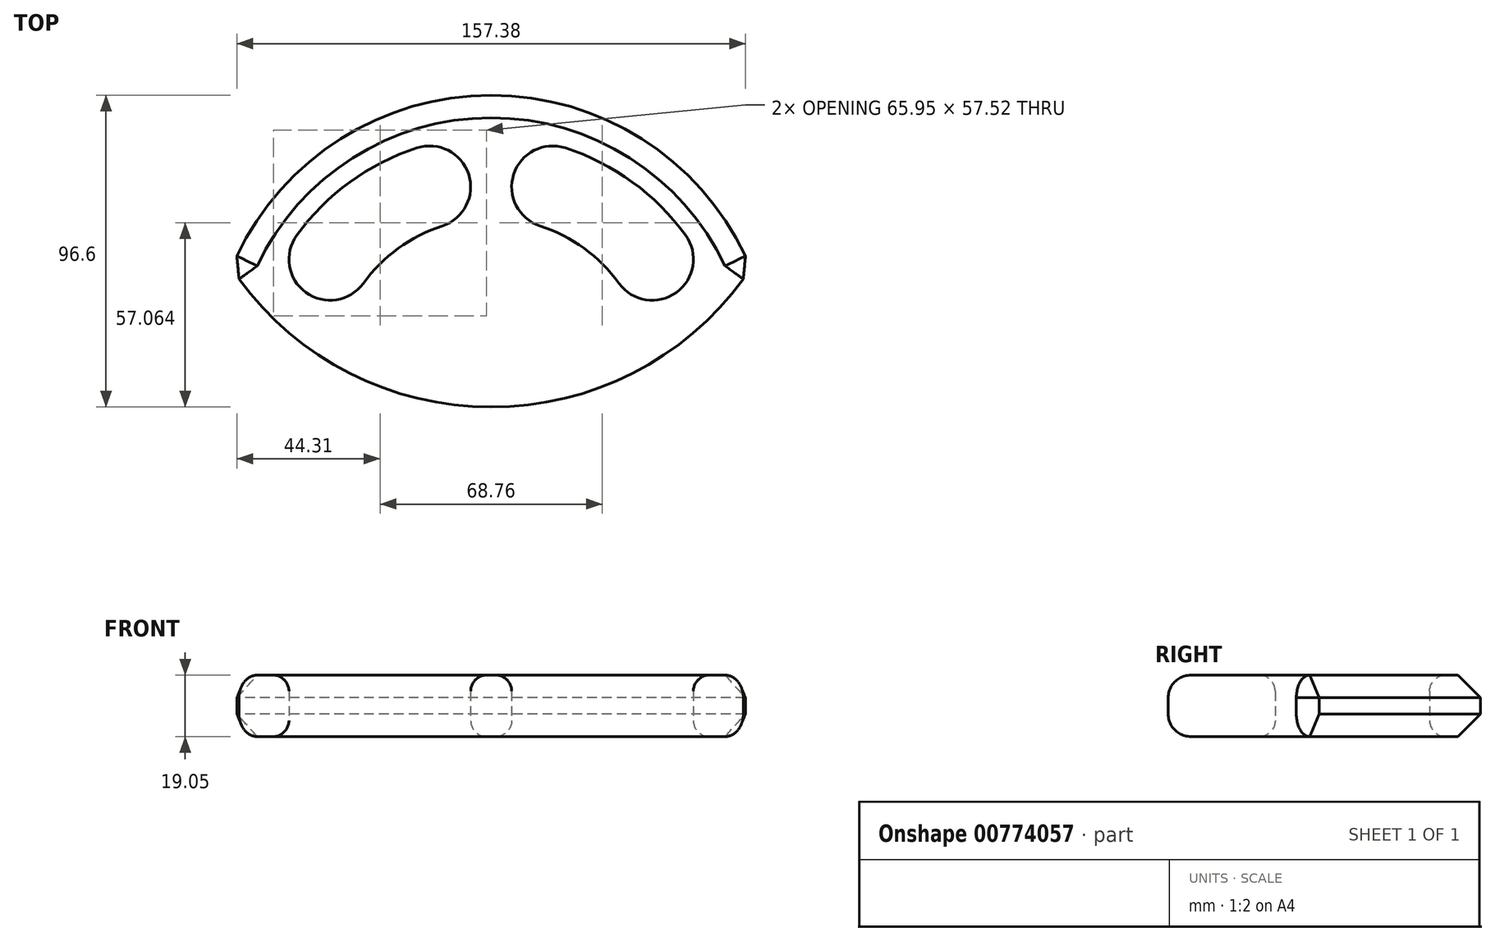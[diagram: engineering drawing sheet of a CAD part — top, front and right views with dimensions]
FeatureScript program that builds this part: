
annotation { "Feature Type Name" : "Feature", "Feature Type Description" : "" }
export const myFeature = defineFeature(function(context is Context, id is Id, definition is map)
    precondition{}
    {
        {
            var Q0;
            Q0=qCreatedBy(makeId("Top.planeOp"),FACE);
            var sketch = newSketch(context, id + "F0", { "sketchPlane" : qUnion([Q0])});
            skCircle(sketch, "E0.cCircle", {"center": v(0, 0) * mm, "radius": 61.65 * mm, "construction": true});
            skLineSegment(sketch, "E0.0", {"start": v(61.65, 0) * mm, "end": v(49.87, -36.24) * mm});
            skLineSegment(sketch, "E0.1", {"start": v(49.87, -36.24) * mm, "end": v(19.05, -58.63) * mm});
            skLineSegment(sketch, "E0.2", {"start": v(19.05, -58.63) * mm, "end": v(-19.05, -58.63) * mm});
            skLineSegment(sketch, "E0.3", {"start": v(-19.05, -58.63) * mm, "end": v(-49.87, -36.24) * mm});
            skLineSegment(sketch, "E0.4", {"start": v(-49.87, -36.24) * mm, "end": v(-61.65, 0) * mm});
            skLineSegment(sketch, "E0.5", {"start": v(-61.65, 0) * mm, "end": v(-49.87, 36.24) * mm});
            skLineSegment(sketch, "E0.6", {"start": v(-49.87, 36.24) * mm, "end": v(-19.05, 58.63) * mm});
            skLineSegment(sketch, "E0.7", {"start": v(-19.05, 58.63) * mm, "end": v(19.05, 58.63) * mm});
            skLineSegment(sketch, "E0.8", {"start": v(19.05, 58.63) * mm, "end": v(49.87, 36.24) * mm});
            skLineSegment(sketch, "E0.9", {"start": v(49.87, 36.24) * mm, "end": v(61.65, 0) * mm});
            skCircle(sketch, "E1", {"center": v(-19.05, 58.63) * mm, "radius": 12.7 * mm});
            skCircle(sketch, "E2", {"center": v(19.05, 58.63) * mm, "radius": 12.7 * mm});
            skCircle(sketch, "E3", {"center": v(-49.87, 36.24) * mm, "radius": 12.7 * mm});
            skCircle(sketch, "E4", {"center": v(49.87, 36.24) * mm, "radius": 12.7 * mm});
            skCircle(sketch, "E5", {"center": v(0, 0) * mm, "radius": 48.95 * mm});
            skCircle(sketch, "E6", {"center": v(0, 0) * mm, "radius": 74.35 * mm});
            skCircle(sketch, "E7", {"center": v(0, 0) * mm, "radius": 87.05 * mm});
            skCircle(sketch, "E8", {"center": v(0, 0) * mm, "radius": 36.25 * mm});
            skCircle(sketch, "E9", {"center": v(-49.87, 36.24) * mm, "radius": 25.4 * mm});
            skCircle(sketch, "E10", {"center": v(49.87, 36.24) * mm, "radius": 25.4 * mm});
            skCircle(sketch, "E11", {"center": v(0, 87.05) * mm, "radius": 96.6 * mm});
            skSolve(sketch);
        }
        {
            var Q0;
            {var subQ0=sQuery(id+"F0.wireOp",EDGE,"E5");var subQ8=makeQuery(id+"F0.imprint","INTERSECT",VERTEX,{"derivedFrom":[sQuery(id+"F0.wireOp",EDGE,"E2"),subQ0]});Q0=makeQuery(id+"F0.imprint","IMPRINT",FACE,{"disambiguationData":[TD([[makeQuery(id+"F0.imprint","IMPRINT",EDGE,{"disambiguationData":[TD([[subQ8,1.0]])],"derivedFrom":subQ0}),1.0]])]});}
            var Q1;
            {var subQ5=sQuery(id+"F0.wireOp",EDGE,"E6");var subQ9=makeQuery(id+"F0.imprint","INTERSECT",VERTEX,{"derivedFrom":[sQuery(id+"F0.wireOp",EDGE,"E2"),subQ5]});Q1=makeQuery(id+"F0.imprint","IMPRINT",FACE,{"disambiguationData":[TD([[makeQuery(id+"F0.imprint","IMPRINT",EDGE,{"disambiguationData":[TD([[subQ9,1.0]])],"derivedFrom":subQ5}),-1.0]])]});}
            var Q2;
            {var subQ0=sQuery(id+"F0.wireOp",EDGE,"E1");var subQ1=sQuery(id+"F0.wireOp",EDGE,"E0.7");var subQ2=makeQuery(id+"F0.imprint","INTERSECT",VERTEX,{"derivedFrom":[subQ1,subQ0]});Q2=makeQuery(id+"F0.imprint","IMPRINT",FACE,{"disambiguationData":[TD([[makeQuery(id+"F0.imprint","IMPRINT",EDGE,{"disambiguationData":[TD([[subQ2,-1.0]])],"derivedFrom":subQ1}),-1.0]])]});}
            var Q3;
            {var subQ0=sQuery(id+"F0.wireOp",EDGE,"E1");var subQ1=sQuery(id+"F0.wireOp",EDGE,"E0.7");var subQ2=makeQuery(id+"F0.imprint","INTERSECT",VERTEX,{"derivedFrom":[subQ1,subQ0]});Q3=makeQuery(id+"F0.imprint","IMPRINT",FACE,{"disambiguationData":[TD([[makeQuery(id+"F0.imprint","IMPRINT",EDGE,{"disambiguationData":[TD([[subQ2,-1.0]])],"derivedFrom":subQ1}),1.0]])]});}
            var Q4;
            {var subQ0=sQuery(id+"F0.wireOp",EDGE,"E5");var subQ1=makeQuery(id+"F0.imprint","INTERSECT",VERTEX,{"derivedFrom":[sQuery(id+"F0.wireOp",EDGE,"E3"),subQ0]});Q4=makeQuery(id+"F0.imprint","IMPRINT",FACE,{"disambiguationData":[TD([[makeQuery(id+"F0.imprint","IMPRINT",EDGE,{"disambiguationData":[TD([[subQ1,1.0]])],"derivedFrom":subQ0}),1.0]])]});}
            var Q5;
            {var subQ0=sQuery(id+"F0.wireOp",EDGE,"E9");var subQ1=sQuery(id+"F0.wireOp",EDGE,"E5");var subQ2=makeQuery(id+"F0.imprint","INTERSECT",VERTEX,{"disambiguationData":[OD(1.0)],"derivedFrom":[subQ1,subQ0]});Q5=makeQuery(id+"F0.imprint","IMPRINT",FACE,{"disambiguationData":[TD([[makeQuery(id+"F0.imprint","IMPRINT",EDGE,{"disambiguationData":[TD([[subQ2,-1.0]])],"derivedFrom":subQ1}),1.0]])]});}
            var Q6;
            {var subQ0=sQuery(id+"F0.wireOp",EDGE,"E9");var subQ1=sQuery(id+"F0.wireOp",EDGE,"E0.5");var subQ2=makeQuery(id+"F0.imprint","INTERSECT",VERTEX,{"derivedFrom":[subQ1,subQ0]});Q6=makeQuery(id+"F0.imprint","IMPRINT",FACE,{"disambiguationData":[TD([[makeQuery(id+"F0.imprint","IMPRINT",EDGE,{"disambiguationData":[TD([[subQ2,-1.0]])],"derivedFrom":subQ1}),-1.0]])]});}
            var Q7;
            {var subQ0=sQuery(id+"F0.wireOp",EDGE,"E9");var subQ6=sQuery(id+"F0.wireOp",EDGE,"E0.5");var subQ8=makeQuery(id+"F0.imprint","INTERSECT",VERTEX,{"derivedFrom":[subQ6,subQ0]});Q7=makeQuery(id+"F0.imprint","IMPRINT",FACE,{"disambiguationData":[TD([[makeQuery(id+"F0.imprint","IMPRINT",EDGE,{"disambiguationData":[TD([[subQ8,-1.0]])],"derivedFrom":subQ6}),1.0]])]});}
            var Q8;
            {var subQ0=sQuery(id+"F0.wireOp",EDGE,"E6");var subQ1=makeQuery(id+"F0.imprint","INTERSECT",VERTEX,{"derivedFrom":[sQuery(id+"F0.wireOp",EDGE,"E3"),subQ0]});Q8=makeQuery(id+"F0.imprint","IMPRINT",FACE,{"disambiguationData":[TD([[makeQuery(id+"F0.imprint","IMPRINT",EDGE,{"disambiguationData":[TD([[subQ1,1.0]])],"derivedFrom":subQ0}),-1.0]])]});}
            var Q9;
            {var subQ0=sQuery(id+"F0.wireOp",EDGE,"E8");var subQ1=makeQuery(id+"F0.imprint","INTERSECT",VERTEX,{"derivedFrom":[subQ0,sQuery(id+"F0.wireOp",EDGE,"E9")]});Q9=makeQuery(id+"F0.imprint","IMPRINT",FACE,{"disambiguationData":[TD([[makeQuery(id+"F0.imprint","IMPRINT",EDGE,{"disambiguationData":[TD([[subQ1,1.0]])],"derivedFrom":subQ0}),1.0]])]});}
            var Q10;
            {var subQ0=sQuery(id+"F0.wireOp",EDGE,"E5");var subQ1=makeQuery(id+"F0.imprint","INTERSECT",VERTEX,{"derivedFrom":[sQuery(id+"F0.wireOp",EDGE,"E4"),subQ0]});Q10=makeQuery(id+"F0.imprint","IMPRINT",FACE,{"disambiguationData":[TD([[makeQuery(id+"F0.imprint","IMPRINT",EDGE,{"disambiguationData":[TD([[subQ1,1.0]])],"derivedFrom":subQ0}),1.0]])]});}
            var Q11;
            {var subQ1=sQuery(id+"F0.wireOp",EDGE,"E0.9");var subQ4=sQuery(id+"F0.wireOp",EDGE,"E4");var subQ5=makeQuery(id+"F0.imprint","INTERSECT",VERTEX,{"derivedFrom":[subQ1,subQ4]});Q11=makeQuery(id+"F0.imprint","IMPRINT",FACE,{"disambiguationData":[TD([[makeQuery(id+"F0.imprint","IMPRINT",EDGE,{"disambiguationData":[TD([[subQ5,-1.0]])],"derivedFrom":subQ1}),1.0]])]});}
            var Q12;
            {var subQ0=sQuery(id+"F0.wireOp",EDGE,"E4");var subQ1=sQuery(id+"F0.wireOp",EDGE,"E0.9");var subQ2=makeQuery(id+"F0.imprint","INTERSECT",VERTEX,{"derivedFrom":[subQ1,subQ0]});Q12=makeQuery(id+"F0.imprint","IMPRINT",FACE,{"disambiguationData":[TD([[makeQuery(id+"F0.imprint","IMPRINT",EDGE,{"disambiguationData":[TD([[subQ2,-1.0]])],"derivedFrom":subQ1}),-1.0]])]});}
            var Q13;
            {var subQ0=sQuery(id+"F0.wireOp",EDGE,"E6");var subQ1=makeQuery(id+"F0.imprint","INTERSECT",VERTEX,{"derivedFrom":[sQuery(id+"F0.wireOp",EDGE,"E4"),subQ0]});Q13=makeQuery(id+"F0.imprint","IMPRINT",FACE,{"disambiguationData":[TD([[makeQuery(id+"F0.imprint","IMPRINT",EDGE,{"disambiguationData":[TD([[subQ1,1.0]])],"derivedFrom":subQ0}),-1.0]])]});}
            var Q14;
            {var subQ0=sQuery(id+"F0.wireOp",EDGE,"E11");var subQ1=sQuery(id+"F0.wireOp",EDGE,"E0.5");var subQ2=makeQuery(id+"F0.imprint","INTERSECT",VERTEX,{"derivedFrom":[subQ1,subQ0]});Q14=makeQuery(id+"F0.imprint","IMPRINT",FACE,{"disambiguationData":[TD([[makeQuery(id+"F0.imprint","IMPRINT",EDGE,{"disambiguationData":[TD([[subQ2,-1.0]])],"derivedFrom":subQ1}),-1.0]])]});}
            var Q15;
            {var subQ0=sQuery(id+"F0.wireOp",EDGE,"E11");var subQ1=sQuery(id+"F0.wireOp",EDGE,"E0.5");var subQ2=makeQuery(id+"F0.imprint","INTERSECT",VERTEX,{"derivedFrom":[subQ1,subQ0]});Q15=makeQuery(id+"F0.imprint","IMPRINT",FACE,{"disambiguationData":[TD([[makeQuery(id+"F0.imprint","IMPRINT",EDGE,{"disambiguationData":[TD([[subQ2,-1.0]])],"derivedFrom":subQ1}),1.0]])]});}
            var Q16;
            {var subQ0=sQuery(id+"F0.wireOp",EDGE,"E10");var subQ1=sQuery(id+"F0.wireOp",EDGE,"E5");var subQ2=makeQuery(id+"F0.imprint","INTERSECT",VERTEX,{"disambiguationData":[OD(0.0)],"derivedFrom":[subQ1,subQ0]});Q16=makeQuery(id+"F0.imprint","IMPRINT",FACE,{"disambiguationData":[TD([[makeQuery(id+"F0.imprint","IMPRINT",EDGE,{"disambiguationData":[TD([[subQ2,1.0]])],"derivedFrom":subQ1}),1.0]])]});}
            var Q17;
            {var subQ0=sQuery(id+"F0.wireOp",EDGE,"E10");var subQ1=sQuery(id+"F0.wireOp",EDGE,"E0.9");var subQ2=makeQuery(id+"F0.imprint","INTERSECT",VERTEX,{"derivedFrom":[subQ1,subQ0]});Q17=makeQuery(id+"F0.imprint","IMPRINT",FACE,{"disambiguationData":[TD([[makeQuery(id+"F0.imprint","IMPRINT",EDGE,{"disambiguationData":[TD([[subQ2,-1.0]])],"derivedFrom":subQ1}),-1.0]])]});}
            var Q18;
            {var subQ0=sQuery(id+"F0.wireOp",EDGE,"E10");var subQ1=sQuery(id+"F0.wireOp",EDGE,"E0.9");var subQ2=makeQuery(id+"F0.imprint","INTERSECT",VERTEX,{"derivedFrom":[subQ1,subQ0]});Q18=makeQuery(id+"F0.imprint","IMPRINT",FACE,{"disambiguationData":[TD([[makeQuery(id+"F0.imprint","IMPRINT",EDGE,{"disambiguationData":[TD([[subQ2,-1.0]])],"derivedFrom":subQ1}),1.0]])]});}
            var Q19;
            {var subQ0=sQuery(id+"F0.wireOp",EDGE,"E10");var subQ1=sQuery(id+"F0.wireOp",EDGE,"E6");var subQ2=makeQuery(id+"F0.imprint","INTERSECT",VERTEX,{"disambiguationData":[OD(0.0)],"derivedFrom":[subQ1,subQ0]});Q19=makeQuery(id+"F0.imprint","IMPRINT",FACE,{"disambiguationData":[TD([[makeQuery(id+"F0.imprint","IMPRINT",EDGE,{"disambiguationData":[TD([[subQ2,1.0]])],"derivedFrom":subQ1}),-1.0]])]});}
            var Q20;
            {var subQ0=sQuery(id+"F0.wireOp",EDGE,"E9");var subQ1=sQuery(id+"F0.wireOp",EDGE,"E6");var subQ2=makeQuery(id+"F0.imprint","INTERSECT",VERTEX,{"disambiguationData":[OD(1.0)],"derivedFrom":[subQ1,subQ0]});Q20=makeQuery(id+"F0.imprint","IMPRINT",FACE,{"disambiguationData":[TD([[makeQuery(id+"F0.imprint","IMPRINT",EDGE,{"disambiguationData":[TD([[subQ2,-1.0]])],"derivedFrom":subQ1}),-1.0]])]});}
            var Q21;
            {var subQ0=sQuery(id+"F0.wireOp",EDGE,"E9");var subQ1=sQuery(id+"F0.wireOp",EDGE,"E6");var subQ2=makeQuery(id+"F0.imprint","INTERSECT",VERTEX,{"disambiguationData":[OD(1.0)],"derivedFrom":[subQ1,subQ0]});Q21=makeQuery(id+"F0.imprint","IMPRINT",FACE,{"disambiguationData":[TD([[makeQuery(id+"F0.imprint","IMPRINT",EDGE,{"disambiguationData":[TD([[subQ2,-1.0]])],"derivedFrom":subQ1}),1.0]])]});}
            var Q22;
            {var subQ0=sQuery(id+"F0.wireOp",EDGE,"E10");var subQ1=sQuery(id+"F0.wireOp",EDGE,"E6");var subQ2=makeQuery(id+"F0.imprint","INTERSECT",VERTEX,{"disambiguationData":[OD(0.0)],"derivedFrom":[subQ1,subQ0]});Q22=makeQuery(id+"F0.imprint","IMPRINT",FACE,{"disambiguationData":[TD([[makeQuery(id+"F0.imprint","IMPRINT",EDGE,{"disambiguationData":[TD([[subQ2,1.0]])],"derivedFrom":subQ1}),1.0]])]});}
            extrude(context, id + "F1", {"entities" : qUnion([Q0, Q1, Q2, Q3, Q4, Q5, Q6, Q7, Q8, Q9, Q10, Q11, Q12, Q13, Q14, Q15, Q16, Q17, Q18, Q19, Q20, Q21, Q22]), "depth" : 19.05 * mm, "offsetDistance" : 25 * mm});
        }
        {
            var Q0;
            Q0=makeQuery(id+"F1.opExtrude","CAP_EDGE",EDGE,{"disambiguationData":[OSD([sQuery(id+"F0.wireOp",EDGE,"E11")])],"isStart":false});
            var Q1;
            Q1=makeQuery(id+"F1.opExtrude","CAP_EDGE",EDGE,{"disambiguationData":[OSD([sQuery(id+"F0.wireOp",EDGE,"E11")])],"isStart":true});
            fillet(context, id + "F2", {"entities" : qUnion([Q0, Q1]), "radius" : 7 * mm, "tangentPropagation" : true, "allowEdgeOverflow" : false});
        }
        {
            var Q0;
            Q0=makeQuery(id+"F1.opExtrude","CAP_EDGE",EDGE,{"disambiguationData":[OSD([sQuery(id+"F0.wireOp",EDGE,"E7")])],"isStart":true});
            var Q1;
            Q1=makeQuery(id+"F1.opExtrude","CAP_EDGE",EDGE,{"disambiguationData":[OSD([sQuery(id+"F0.wireOp",EDGE,"E7")])],"isStart":false});
            chamfer(context, id + "F3", {"entities" : qUnion([Q0, Q1]), "width" : 7 * mm, "tangentPropagation" : true});
        }
        {
            var Q0;
            {var subQ0=sQuery(id+"F0.wireOp",EDGE,"E5");Q0=makeQuery(id+"F1.opExtrude","CAP_EDGE",EDGE,{"disambiguationData":[OSD([subQ0]),TDD([makeQuery(id+"F0.imprint","IMPRINT",EDGE,{"disambiguationData":[TD([[makeQuery(id+"F0.imprint","INTERSECT",VERTEX,{"derivedFrom":[sQuery(id+"F0.wireOp",EDGE,"E1"),subQ0]}),-1.0]])],"derivedFrom":subQ0}),makeQuery(id+"F0.imprint","IMPRINT",EDGE,{"disambiguationData":[TD([[makeQuery(id+"F0.imprint","INTERSECT",VERTEX,{"derivedFrom":[sQuery(id+"F0.wireOp",EDGE,"E3"),subQ0]}),1.0]])],"derivedFrom":subQ0})])],"isStart":false});}
            var Q1;
            {var subQ0=sQuery(id+"F0.wireOp",EDGE,"E6");Q1=makeQuery(id+"F1.opExtrude","CAP_EDGE",EDGE,{"disambiguationData":[OSD([subQ0]),TDD([makeQuery(id+"F0.imprint","IMPRINT",EDGE,{"disambiguationData":[TD([[makeQuery(id+"F0.imprint","INTERSECT",VERTEX,{"derivedFrom":[sQuery(id+"F0.wireOp",EDGE,"E1"),subQ0]}),-1.0]])],"derivedFrom":subQ0}),makeQuery(id+"F0.imprint","IMPRINT",EDGE,{"disambiguationData":[TD([[makeQuery(id+"F0.imprint","INTERSECT",VERTEX,{"derivedFrom":[sQuery(id+"F0.wireOp",EDGE,"E3"),subQ0]}),1.0]])],"derivedFrom":subQ0})])],"isStart":false});}
            var Q2;
            Q2=makeQuery(id+"F1.opExtrude","CAP_EDGE",EDGE,{"disambiguationData":[OSD([sQuery(id+"F0.wireOp",EDGE,"E1")])],"isStart":false});
            var Q3;
            Q3=makeQuery(id+"F1.opExtrude","CAP_EDGE",EDGE,{"disambiguationData":[OSD([sQuery(id+"F0.wireOp",EDGE,"E1")])],"isStart":true});
            var Q4;
            {var subQ0=sQuery(id+"F0.wireOp",EDGE,"E6");Q4=makeQuery(id+"F1.opExtrude","CAP_EDGE",EDGE,{"disambiguationData":[OSD([subQ0]),TDD([makeQuery(id+"F0.imprint","IMPRINT",EDGE,{"disambiguationData":[TD([[makeQuery(id+"F0.imprint","INTERSECT",VERTEX,{"derivedFrom":[sQuery(id+"F0.wireOp",EDGE,"E1"),subQ0]}),-1.0]])],"derivedFrom":subQ0}),makeQuery(id+"F0.imprint","IMPRINT",EDGE,{"disambiguationData":[TD([[makeQuery(id+"F0.imprint","INTERSECT",VERTEX,{"derivedFrom":[sQuery(id+"F0.wireOp",EDGE,"E3"),subQ0]}),1.0]])],"derivedFrom":subQ0})])],"isStart":true});}
            var Q5;
            Q5=makeQuery(id+"F1.opExtrude","CAP_EDGE",EDGE,{"disambiguationData":[OSD([sQuery(id+"F0.wireOp",EDGE,"E3")])],"isStart":false});
            var Q6;
            Q6=makeQuery(id+"F1.opExtrude","CAP_EDGE",EDGE,{"disambiguationData":[OSD([sQuery(id+"F0.wireOp",EDGE,"E3")])],"isStart":true});
            var Q7;
            {var subQ0=sQuery(id+"F0.wireOp",EDGE,"E5");Q7=makeQuery(id+"F1.opExtrude","CAP_EDGE",EDGE,{"disambiguationData":[OSD([subQ0]),TDD([makeQuery(id+"F0.imprint","IMPRINT",EDGE,{"disambiguationData":[TD([[makeQuery(id+"F0.imprint","INTERSECT",VERTEX,{"derivedFrom":[sQuery(id+"F0.wireOp",EDGE,"E1"),subQ0]}),-1.0]])],"derivedFrom":subQ0}),makeQuery(id+"F0.imprint","IMPRINT",EDGE,{"disambiguationData":[TD([[makeQuery(id+"F0.imprint","INTERSECT",VERTEX,{"derivedFrom":[sQuery(id+"F0.wireOp",EDGE,"E3"),subQ0]}),1.0]])],"derivedFrom":subQ0})])],"isStart":true});}
            var Q8;
            {var subQ0=sQuery(id+"F0.wireOp",EDGE,"E5");Q8=makeQuery(id+"F1.opExtrude","CAP_EDGE",EDGE,{"disambiguationData":[OSD([subQ0]),TDD([makeQuery(id+"F0.imprint","IMPRINT",EDGE,{"disambiguationData":[TD([[makeQuery(id+"F0.imprint","INTERSECT",VERTEX,{"derivedFrom":[sQuery(id+"F0.wireOp",EDGE,"E4"),subQ0]}),-1.0]])],"derivedFrom":subQ0}),makeQuery(id+"F0.imprint","IMPRINT",EDGE,{"disambiguationData":[TD([[makeQuery(id+"F0.imprint","INTERSECT",VERTEX,{"derivedFrom":[sQuery(id+"F0.wireOp",EDGE,"E2"),subQ0]}),1.0]])],"derivedFrom":subQ0})])],"isStart":true});}
            var Q9;
            Q9=makeQuery(id+"F1.opExtrude","CAP_EDGE",EDGE,{"disambiguationData":[OSD([sQuery(id+"F0.wireOp",EDGE,"E2")])],"isStart":true});
            var Q10;
            Q10=makeQuery(id+"F1.opExtrude","CAP_EDGE",EDGE,{"disambiguationData":[OSD([sQuery(id+"F0.wireOp",EDGE,"E4")])],"isStart":true});
            var Q11;
            {var subQ0=sQuery(id+"F0.wireOp",EDGE,"E6");Q11=makeQuery(id+"F1.opExtrude","CAP_EDGE",EDGE,{"disambiguationData":[OSD([subQ0]),TDD([makeQuery(id+"F0.imprint","IMPRINT",EDGE,{"disambiguationData":[TD([[makeQuery(id+"F0.imprint","INTERSECT",VERTEX,{"derivedFrom":[sQuery(id+"F0.wireOp",EDGE,"E4"),subQ0]}),-1.0]])],"derivedFrom":subQ0}),makeQuery(id+"F0.imprint","IMPRINT",EDGE,{"disambiguationData":[TD([[makeQuery(id+"F0.imprint","INTERSECT",VERTEX,{"derivedFrom":[sQuery(id+"F0.wireOp",EDGE,"E2"),subQ0]}),1.0]])],"derivedFrom":subQ0})])],"isStart":true});}
            var Q12;
            Q12=makeQuery(id+"F1.opExtrude","CAP_EDGE",EDGE,{"disambiguationData":[OSD([sQuery(id+"F0.wireOp",EDGE,"E2")])],"isStart":false});
            var Q13;
            {var subQ0=sQuery(id+"F0.wireOp",EDGE,"E6");Q13=makeQuery(id+"F1.opExtrude","CAP_EDGE",EDGE,{"disambiguationData":[OSD([subQ0]),TDD([makeQuery(id+"F0.imprint","IMPRINT",EDGE,{"disambiguationData":[TD([[makeQuery(id+"F0.imprint","INTERSECT",VERTEX,{"derivedFrom":[sQuery(id+"F0.wireOp",EDGE,"E4"),subQ0]}),-1.0]])],"derivedFrom":subQ0}),makeQuery(id+"F0.imprint","IMPRINT",EDGE,{"disambiguationData":[TD([[makeQuery(id+"F0.imprint","INTERSECT",VERTEX,{"derivedFrom":[sQuery(id+"F0.wireOp",EDGE,"E2"),subQ0]}),1.0]])],"derivedFrom":subQ0})])],"isStart":false});}
            var Q14;
            {var subQ0=sQuery(id+"F0.wireOp",EDGE,"E5");Q14=makeQuery(id+"F1.opExtrude","CAP_EDGE",EDGE,{"disambiguationData":[OSD([subQ0]),TDD([makeQuery(id+"F0.imprint","IMPRINT",EDGE,{"disambiguationData":[TD([[makeQuery(id+"F0.imprint","INTERSECT",VERTEX,{"derivedFrom":[sQuery(id+"F0.wireOp",EDGE,"E4"),subQ0]}),-1.0]])],"derivedFrom":subQ0}),makeQuery(id+"F0.imprint","IMPRINT",EDGE,{"disambiguationData":[TD([[makeQuery(id+"F0.imprint","INTERSECT",VERTEX,{"derivedFrom":[sQuery(id+"F0.wireOp",EDGE,"E2"),subQ0]}),1.0]])],"derivedFrom":subQ0})])],"isStart":false});}
            var Q15;
            Q15=makeQuery(id+"F1.opExtrude","CAP_EDGE",EDGE,{"disambiguationData":[OSD([sQuery(id+"F0.wireOp",EDGE,"E4")])],"isStart":false});
            fillet(context, id + "F4", {"entities" : qUnion([Q0, Q1, Q2, Q3, Q4, Q5, Q6, Q7, Q8, Q9, Q10, Q11, Q12, Q13, Q14, Q15]), "radius" : 5 * mm, "tangentPropagation" : true, "allowEdgeOverflow" : false});
        }
    });
